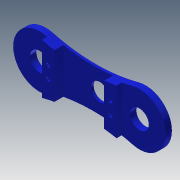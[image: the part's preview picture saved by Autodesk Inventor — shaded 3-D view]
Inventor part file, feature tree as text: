
AUTODESK INVENTOR PART (.ipt)
format: ipt  version: 2013 (Build 170138000, 138)  size: 451,072 bytes
history: native  units: mm
features: extrude x34, sketch x34
ambient origin geometry x8: Origin, YZ Plane, XZ Plane, XY Plane, X Axis, Y Axis, Z Axis, Center Point
bodies: Solid1 (feature_tree)
feature tree (68):
  extrude  "Extrusion1"  Depth=2.0mm TaperAngle=0.0deg
  extrude  "Extrusion2"  Depth=3.0mm
  extrude  "Extrusion3"  Depth=2.0mm TaperAngle=0.0deg
  extrude  "Extrusion4"  Depth=6.0mm
  extrude  "Extrusion5"  Depth=3.0mm
  extrude  "Extrusion6"  Depth=3.0mm
  extrude  "Extrusion7"  Depth=29.5mm
  extrude  "Extrusion8"  Depth=40.2mm
  extrude  "Extrusion9"  Depth=3.0mm
  extrude  "Extrusion10"  Depth=40.2mm
  extrude  "Extrusion11"  Depth=2.0mm TaperAngle=0.0deg
  extrude  "Extrusion12"  Depth=49.7mm
  extrude  "Extrusion13"  Depth=3.0mm
  sketch  "Sketch14"  dims[d74=3.0mm d75=2.0mm d76=0.0mm]
  sketch  "Sketch15"  dims[d77=2.0mm d78=0.0mm d79=2.0mm d80=0.0mm]
  sketch  "Sketch16"  dims[d81=2.0mm d82=0.0mm d83=2.0mm d84=0.0mm]
  extrude  "Extrusion14"  Depth=2.0mm TaperAngle=0.0deg
  extrude  "Extrusion15"  Depth=2.0mm TaperAngle=0.0deg
  extrude  "Extrusion16"  Depth=2.0mm TaperAngle=0.0deg
  extrude  "Extrusion17"  Depth=2.0mm TaperAngle=0.0deg
  extrude  "Extrusion18"  Depth=2.0mm TaperAngle=0.0deg
  extrude  "Extrusion19"  Depth=6.0mm
  extrude  "Extrusion20"  Depth=34.65mm
  extrude  "Extrusion21"  Depth=20.0mm
  extrude  "Extrusion22"  Depth=3.0mm
  extrude  "Extrusion23"  Depth=49.7mm
  extrude  "Extrusion24"  Depth=3.0mm
  extrude  "Extrusion25"  Depth=6.0mm
  extrude  "Extrusion26"  Depth=2.0mm TaperAngle=0.0deg
  extrude  "Extrusion27"  Depth=10.0mm
  extrude  "Extrusion28"  Depth=4.1mm TaperAngle=0.0deg
  extrude  "Extrusion29"  Depth=15.0mm
  extrude  "Extrusion30"  Depth=5.0mm TaperAngle=0.0deg
  extrude  "Extrusion31"  Depth=6.0mm
  extrude  "Extrusion32"  Depth=5.0mm TaperAngle=0.0deg
  extrude  "Extrusion33"  Depth=6.0mm
  extrude  "Extrusion34"  Depth=14.0mm
  sketch  "Sketch1"  dims[d1=6.0mm d3=10.0mm d5=4.0mm d7=4.0mm d8=2.0mm d9=0.0mm]
  sketch  "Sketch2"  dims[d11=3.0mm d14=3.0mm]
  sketch  "Sketch3"  dims[d15=3.0mm d16=2.0mm d17=0.0mm]
  sketch  "Sketch4"  dims[d18=10.5mm d19=6.0mm]
  sketch  "Sketch5"  dims[d20=2.0mm d21=0.0mm d33=3.0mm]
  sketch  "Sketch6"  dims[d34=3.0mm d35=3.0mm]
  sketch  "Sketch7"  dims[d36=2.0mm d37=0.0mm d46=29.5mm]
  sketch  "Sketch8"  dims[d48=10.7mm d49=40.2mm]
  sketch  "Sketch9"  dims[d57=3.0mm d58=3.0mm]
  sketch  "Sketch10"  dims[d63=2.0mm d64=0.0mm d65=40.2mm]
  sketch  "Sketch11"  dims[d66=20.0mm d67=2.0mm d68=0.0mm]
  sketch  "Sketch12"  dims[d69=2.0mm d70=0.0mm d71=49.7mm]
  sketch  "Sketch13"  dims[d72=49.7mm d73=3.0mm]
  sketch  "Sketch17"  dims[d85=2.0mm d86=0.0mm d87=2.0mm d88=0.0mm]
  sketch  "Sketch18"  dims[d89=2.0mm d90=0.0mm d91=2.0mm d92=0.0mm]
  sketch  "Sketch19"  dims[d93=2.0mm d94=0.0mm d95=6.0mm]
  sketch  "Sketch20"  dims[d96=2.0mm d97=0.0mm d100=34.65mm]
  sketch  "Sketch21"  dims[d103=40.2mm d104=20.0mm]
  sketch  "Sketch22"  dims[d109=3.0mm d110=3.0mm]
  sketch  "Sketch23"  dims[d111=49.7mm d112=49.7mm]
  sketch  "Sketch24"  dims[d113=3.0mm d114=3.0mm]
  sketch  "Sketch25"  dims[d115=2.0mm d116=0.0mm d117=6.0mm]
  sketch  "Sketch26"  dims[d118=2.0mm d119=0.0mm d120=2.0mm d121=0.0mm]
  sketch  "Sketch27"  dims[d122=3.0mm d123=0.0mm d124=10.0mm]
  sketch  "Sketch28"  dims[d125=10.0mm d126=4.1mm d127=0.0mm]
  sketch  "Sketch29"  dims[d128=4.1mm d129=0.0mm d130=15.0mm]
  sketch  "Sketch30"  dims[d131=15.0mm d132=5.0mm d133=0.0mm]
  sketch  "Sketch31"  dims[d134=15.45mm d135=6.0mm]
  sketch  "Sketch32"  dims[d136=5.0mm d137=0.0mm d138=5.0mm d139=0.0mm]
  sketch  "Sketch33"  dims[d140=15.45mm d141=6.0mm]
  sketch  "Sketch34"  dims[d142=5.0mm d143=0.0mm d144=14.0mm d145=5.0mm d146=0.0mm d147=3.0mm d148=0.0mm d149=1.0mm d150=0.0mm d151=1.0mm d152=0.0mm d153=4.1mm d154=0.0mm d155=4.1mm d156=0.0mm]
